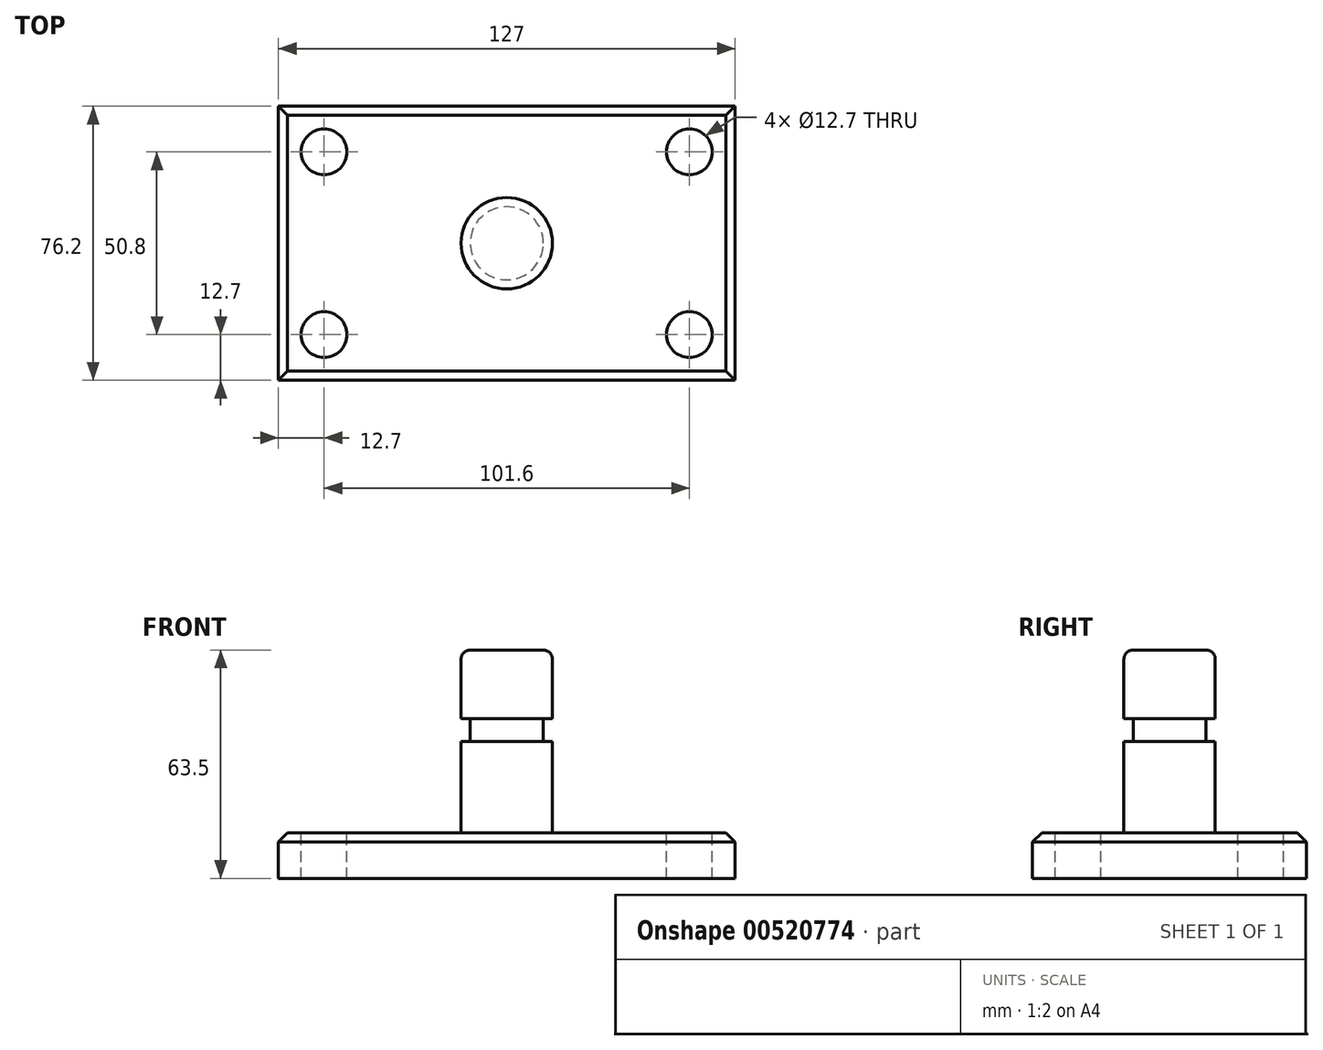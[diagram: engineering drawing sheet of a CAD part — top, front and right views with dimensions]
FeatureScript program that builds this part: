
annotation { "Feature Type Name" : "Feature", "Feature Type Description" : "" }
export const myFeature = defineFeature(function(context is Context, id is Id, definition is map)
    precondition{}
    {
        {
            var Q0;
            Q0=qCreatedBy(makeId("Top.planeOp"),FACE);
            var sketch = newSketch(context, id + "F0", { "sketchPlane" : qUnion([Q0])});
            skLineSegment(sketch, "E0.bottom", {"start": v(63.5, 38.1) * mm, "end": v(-63.5, 38.1) * mm});
            skLineSegment(sketch, "E0.top", {"start": v(63.5, -38.1) * mm, "end": v(-63.5, -38.1) * mm});
            skLineSegment(sketch, "E0.left", {"start": v(63.5, 38.1) * mm, "end": v(63.5, -38.1) * mm});
            skLineSegment(sketch, "E0.right", {"start": v(-63.5, 38.1) * mm, "end": v(-63.5, -38.1) * mm});
            skPoint(sketch, "E0.middle", {"position": v(0, 0) * mm});
            skSolve(sketch);
        }
        {
            var Q0;
            Q0=makeQuery(id+"F0.imprint","IMPRINT",FACE,{"disambiguationData":[TD([[makeQuery(id+"F0.imprint","IMPRINT",EDGE,{"derivedFrom":sQuery(id+"F0.wireOp",EDGE,"E0.bottom")}),1.0]])]});
            extrude(context, id + "F1", {"entities" : qUnion([Q0]), "depth" : 12.7 * mm, "offsetDistance" : 25.4 * mm});
        }
        {
            var Q0;
            Q0=makeQuery(id+"F1.opExtrude","CAP_FACE",FACE,{"disambiguationData":[OSD([sQuery(id+"F0.wireOp",EDGE,"E0.bottom"),sQuery(id+"F0.wireOp",EDGE,"E0.top"),sQuery(id+"F0.wireOp",EDGE,"E0.left"),sQuery(id+"F0.wireOp",EDGE,"E0.right")])],"isStart":false});
            var sketch = newSketch(context, id + "F2", { "sketchPlane" : qUnion([Q0])});
            skCircle(sketch, "E1", {"center": v(-50.8, -25.4) * mm, "radius": 6.35 * mm});
            skCircle(sketch, "E2", {"center": v(-50.8, 25.4) * mm, "radius": 6.35 * mm});
            skCircle(sketch, "E3", {"center": v(50.8, 25.4) * mm, "radius": 6.35 * mm});
            skCircle(sketch, "E4", {"center": v(50.8, -25.4) * mm, "radius": 6.35 * mm});
            skSolve(sketch);
        }
        {
            var Q0;
            Q0=makeQuery(id+"F2.imprint","IMPRINT",FACE,{"disambiguationData":[TD([[makeQuery(id+"F2.imprint","IMPRINT",EDGE,{"derivedFrom":sQuery(id+"F2.wireOp",EDGE,"E1")}),1.0]])]});
            var Q1;
            Q1=makeQuery(id+"F2.imprint","IMPRINT",FACE,{"disambiguationData":[TD([[makeQuery(id+"F2.imprint","IMPRINT",EDGE,{"derivedFrom":sQuery(id+"F2.wireOp",EDGE,"E3")}),1.0]])]});
            var Q2;
            Q2=makeQuery(id+"F2.imprint","IMPRINT",FACE,{"disambiguationData":[TD([[makeQuery(id+"F2.imprint","IMPRINT",EDGE,{"derivedFrom":sQuery(id+"F2.wireOp",EDGE,"E4")}),1.0]])]});
            var Q3;
            Q3=makeQuery(id+"F2.imprint","IMPRINT",FACE,{"disambiguationData":[TD([[makeQuery(id+"F2.imprint","IMPRINT",EDGE,{"derivedFrom":sQuery(id+"F2.wireOp",EDGE,"E2")}),1.0]])]});
            extrude(context, id + "F3", {"entities" : qUnion([Q0, Q1, Q2, Q3]), "operationType" : NewBodyOperationType.REMOVE, "endBound" : BoundingType.THROUGH_ALL, "oppositeDirection" : true, "depth" : 25.4 * mm, "offsetDistance" : 25.4 * mm});
        }
        {
            var Q0;
            Q0=qCreatedBy(makeId("Front.planeOp"),FACE);
            var sketch = newSketch(context, id + "F4", { "sketchPlane" : qUnion([Q0])});
            skLineSegment(sketch, "E5.bottom", {"start": v(0, 12.7) * mm, "end": v(12.7, 12.7) * mm});
            skLineSegment(sketch, "E5.top", {"start": v(0, 63.5) * mm, "end": v(12.7, 63.5) * mm});
            skLineSegment(sketch, "E5.left", {"start": v(0, 12.7) * mm, "end": v(0, 63.5) * mm});
            skLineSegment(sketch, "E5.right", {"start": v(12.7, 12.7) * mm, "end": v(12.7, 63.5) * mm});
            skSolve(sketch);
        }
        {
            var Q0;
            Q0=makeQuery(id+"F4.imprint","IMPRINT",FACE,{"disambiguationData":[TD([[makeQuery(id+"F4.imprint","IMPRINT",EDGE,{"derivedFrom":sQuery(id+"F4.wireOp",EDGE,"E5.bottom")}),1.0]])]});
            var Q1;
            Q1=sQuery(id+"F4.wireOp",EDGE,"E5.left");
            var Q2;
            Q2=sQuery(id+"F4.wireOp",EDGE,"E5.left");
            revolve(context, id + "F5", {"operationType" : NewBodyOperationType.ADD, "entities" : qUnion([Q0]), "surfaceEntities" : qUnion([Q1]), "axis" : qUnion([Q2]), "revolveType" : RevolveType.FULL});
        }
        {
            var Q0;
            Q0=qCreatedBy(makeId("Front.planeOp"),FACE);
            var sketch = newSketch(context, id + "F6", { "sketchPlane" : qUnion([Q0])});
            skLineSegment(sketch, "E6.bottom", {"start": v(10.16, 44.45) * mm, "end": v(25.68, 44.45) * mm});
            skLineSegment(sketch, "E6.top", {"start": v(10.16, 38.1) * mm, "end": v(25.68, 38.1) * mm});
            skLineSegment(sketch, "E6.left", {"start": v(10.16, 44.45) * mm, "end": v(10.16, 38.1) * mm});
            skLineSegment(sketch, "E6.right", {"start": v(25.68, 44.45) * mm, "end": v(25.68, 38.1) * mm});
            skSolve(sketch);
        }
        {
            var Q0;
            Q0=makeQuery(id+"F6.imprint","IMPRINT",FACE,{"disambiguationData":[TD([[makeQuery(id+"F6.imprint","IMPRINT",EDGE,{"derivedFrom":sQuery(id+"F6.wireOp",EDGE,"E6.bottom")}),-1.0]])]});
            var Q1;
            Q1=makeQuery(id+"F5.opRevolve","SWEPT_FACE",FACE,{"disambiguationData":[OSD([sQuery(id+"F4.wireOp",EDGE,"E5.right")])]});
            revolve(context, id + "F7", {"operationType" : NewBodyOperationType.REMOVE, "entities" : qUnion([Q0]), "axis" : qUnion([Q1]), "revolveType" : RevolveType.FULL, "oppositeDirection" : true});
        }
        {
            var Q0;
            Q0=makeQuery(id+"F1.opExtrude","CAP_EDGE",EDGE,{"disambiguationData":[OSD([sQuery(id+"F0.wireOp",EDGE,"E0.top")])],"isStart":false});
            var Q1;
            Q1=makeQuery(id+"F1.opExtrude","CAP_EDGE",EDGE,{"disambiguationData":[OSD([sQuery(id+"F0.wireOp",EDGE,"E0.left")])],"isStart":false});
            var Q2;
            Q2=makeQuery(id+"F1.opExtrude","CAP_EDGE",EDGE,{"disambiguationData":[OSD([sQuery(id+"F0.wireOp",EDGE,"E0.bottom")])],"isStart":false});
            var Q3;
            Q3=makeQuery(id+"F1.opExtrude","CAP_EDGE",EDGE,{"disambiguationData":[OSD([sQuery(id+"F0.wireOp",EDGE,"E0.right")])],"isStart":false});
            chamfer(context, id + "F8", {"entities" : qUnion([Q0, Q1, Q2, Q3]), "width" : 2.54 * mm, "tangentPropagation" : true});
        }
        {
            var Q0;
            Q0=makeQuery(id+"F5.opRevolve","SWEPT_EDGE",EDGE,{"disambiguationData":[OSD([sQuery(id+"F4.wireOp",EDGE,"E5.bottom"),sQuery(id+"F4.wireOp",EDGE,"E5.right")])]});
            var Q1;
            Q1=makeQuery(id+"F5.opRevolve","SWEPT_EDGE",EDGE,{"disambiguationData":[OSD([sQuery(id+"F4.wireOp",EDGE,"E5.top"),sQuery(id+"F4.wireOp",EDGE,"E5.right")])]});
            fillet(context, id + "F9", {"entities" : qUnion([Q0, Q1]), "radius" : 2.54 * mm, "tangentPropagation" : true, "allowEdgeOverflow" : false});
        }
    });
